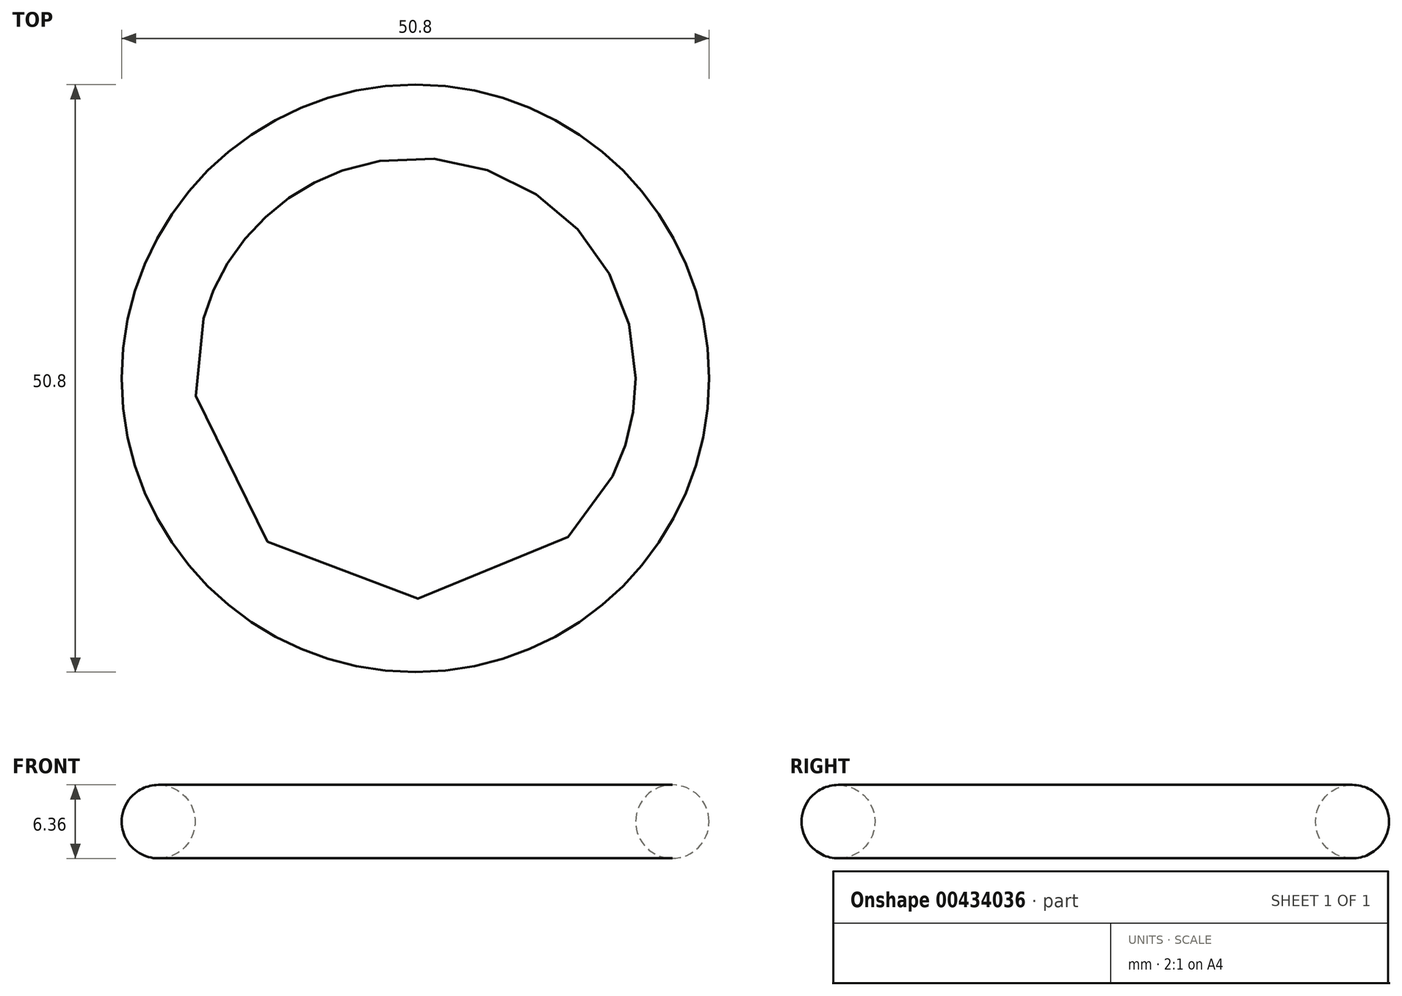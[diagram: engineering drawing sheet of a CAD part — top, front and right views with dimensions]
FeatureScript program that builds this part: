
annotation { "Feature Type Name" : "Feature", "Feature Type Description" : "" }
export const myFeature = defineFeature(function(context is Context, id is Id, definition is map)
    precondition{}
    {
        {
            var Q0;
            Q0=qCreatedBy(makeId("Front.planeOp"),FACE);
            var sketch = newSketch(context, id + "F0", { "sketchPlane" : qUnion([Q0])});
            skCircle(sketch, "E0", {"center": v(-22.22, 0) * mm, "radius": 3.17 * mm});
            skLineSegment(sketch, "E1", {"start": v(0, 22.28) * mm, "end": v(0, -16.7) * mm, "construction": true});
            skSolve(sketch);
        }
        {
            var Q0;
            Q0 = qSketchRegion(id + "F0", true);
            var Q1;
            Q1=sQuery(id+"F0.wireOp",EDGE,"E1");
            revolve(context, id + "F1", {"entities" : qUnion([Q0]), "axis" : qUnion([Q1]), "revolveType" : RevolveType.FULL});
        }
    });
